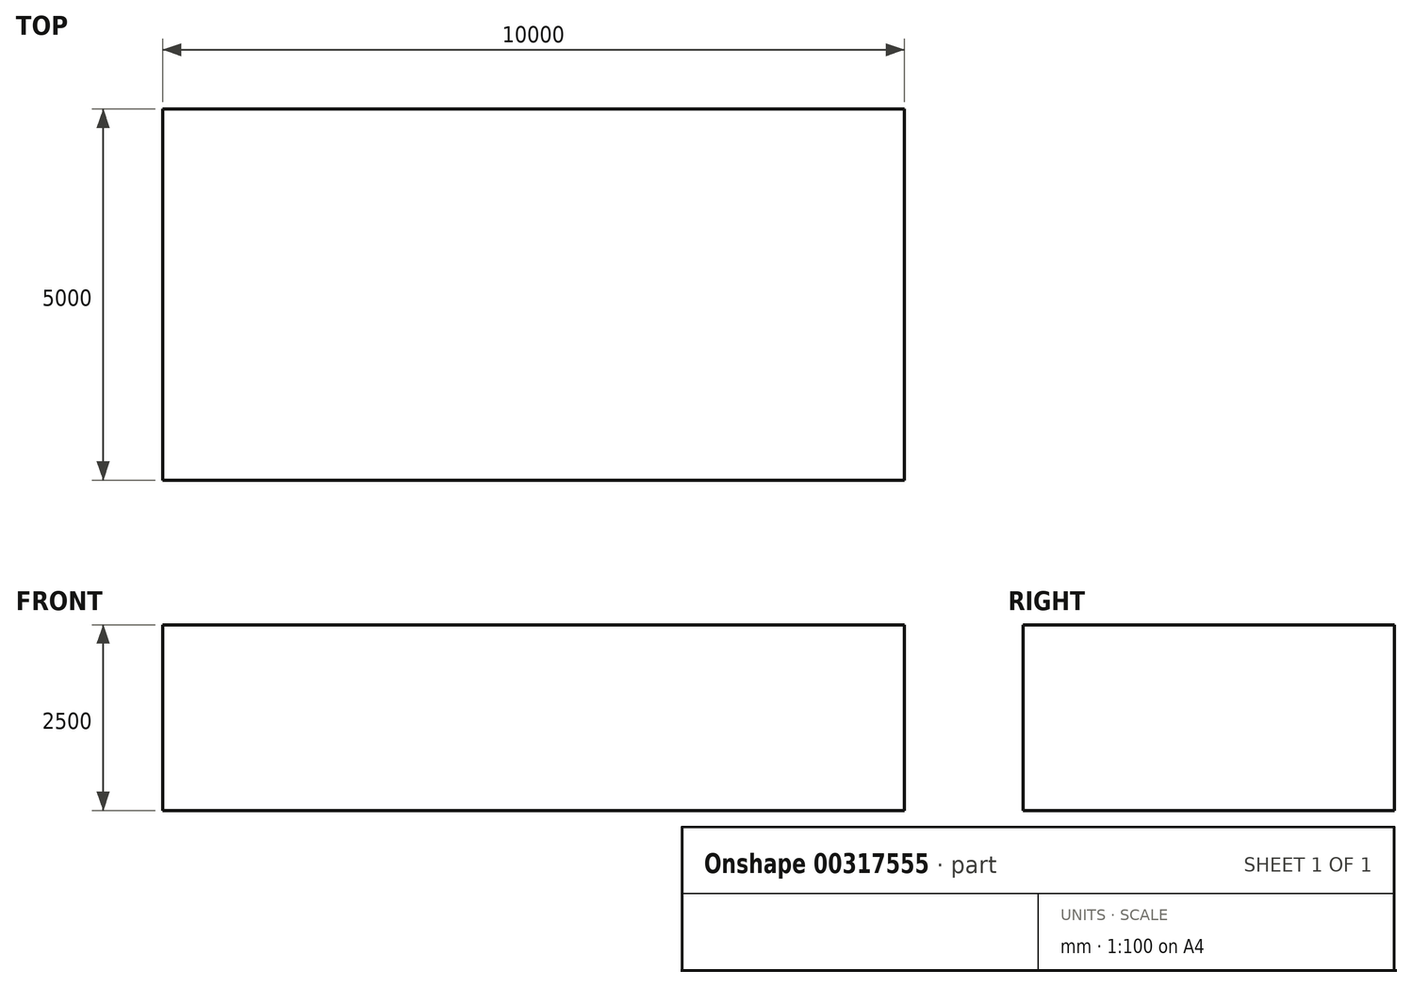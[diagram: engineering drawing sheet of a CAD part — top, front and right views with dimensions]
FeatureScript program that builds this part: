
annotation { "Feature Type Name" : "Feature", "Feature Type Description" : "" }
export const myFeature = defineFeature(function(context is Context, id is Id, definition is map)
    precondition{}
    {
        {
            var Q0;
            Q0=qCreatedBy(makeId("Front.planeOp"),FACE);
            var sketch = newSketch(context, id + "F0", { "sketchPlane" : qUnion([Q0])});
            skLineSegment(sketch, "E0.bottom", {"start": v(-4999.32, 192.92) * mm, "end": v(5000.68, 192.92) * mm});
            skLineSegment(sketch, "E0.top", {"start": v(-4999.32, -2307.08) * mm, "end": v(5000.68, -2307.08) * mm});
            skLineSegment(sketch, "E0.left", {"start": v(-4999.32, 192.92) * mm, "end": v(-4999.32, -2307.08) * mm});
            skLineSegment(sketch, "E0.right", {"start": v(5000.68, 192.92) * mm, "end": v(5000.68, -2307.08) * mm});
            skSolve(sketch);
        }
        {
            var Q0;
            Q0 = qSketchRegion(id + "F0", true);
            extrude(context, id + "F1", {"entities" : qUnion([Q0]), "depth" : 5000 * mm});
        }
    });
